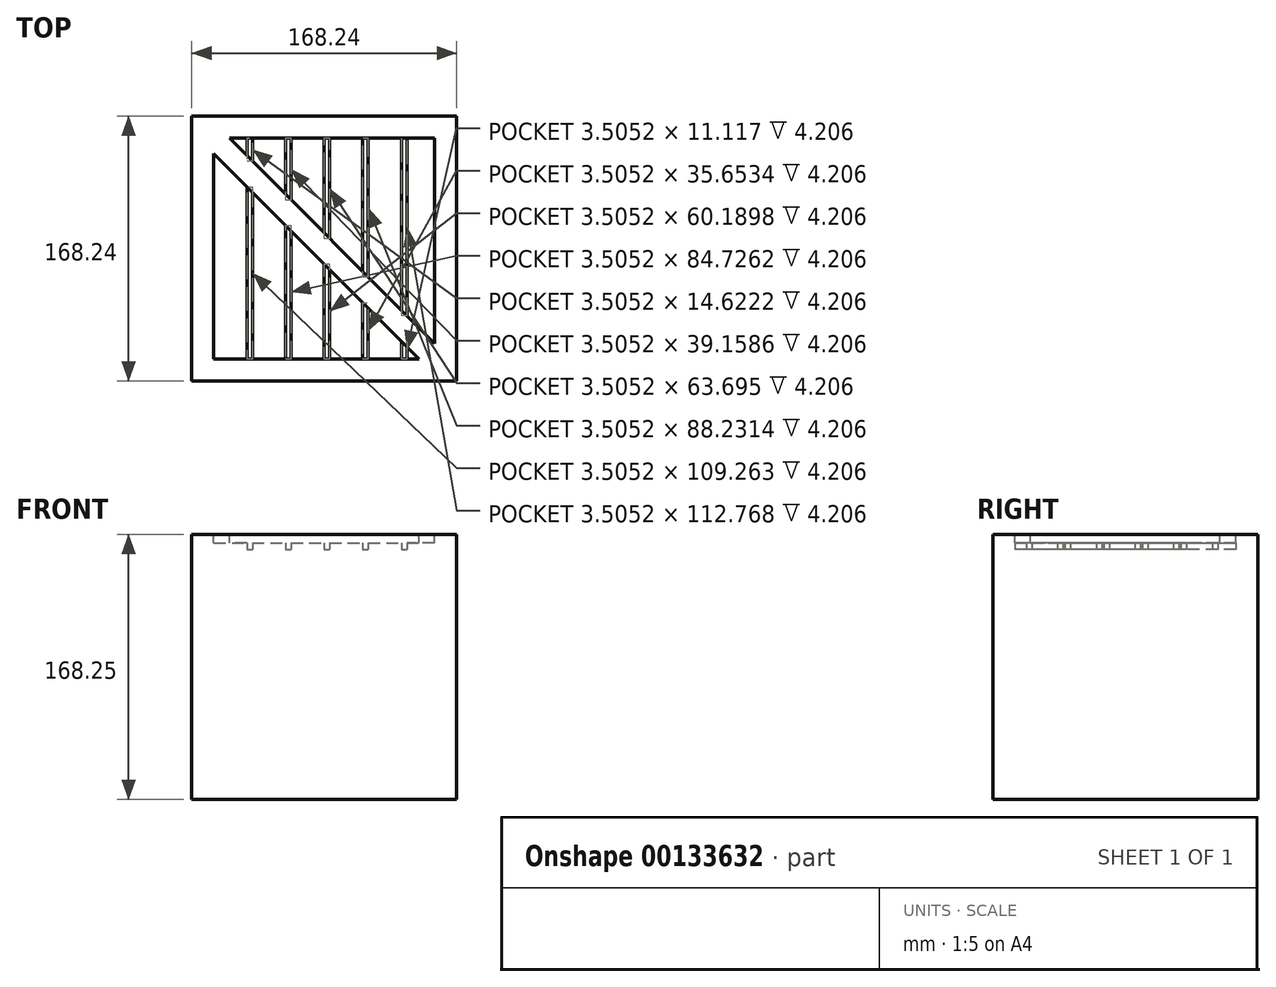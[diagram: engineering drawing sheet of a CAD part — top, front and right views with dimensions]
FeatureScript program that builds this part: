
annotation { "Feature Type Name" : "Feature", "Feature Type Description" : "" }
export const myFeature = defineFeature(function(context is Context, id is Id, definition is map)
    precondition{}
    {
        {
            var Q0;
            Q0=qCreatedBy(makeId("Top.planeOp"),FACE);
            var sketch = newSketch(context, id + "F0", { "sketchPlane" : qUnion([Q0])});
            skLineSegment(sketch, "E0.bottom", {"start": v(609.6, 609.6) * mm, "end": v(-609.6, 609.6) * mm});
            skLineSegment(sketch, "E0.top", {"start": v(609.6, -609.6) * mm, "end": v(-609.6, -609.6) * mm});
            skLineSegment(sketch, "E0.left", {"start": v(609.6, 609.6) * mm, "end": v(609.6, -609.6) * mm});
            skLineSegment(sketch, "E0.right", {"start": v(-609.6, 609.6) * mm, "end": v(-609.6, -609.6) * mm});
            skPoint(sketch, "E0.middle", {"position": v(0, 0) * mm});
            skSolve(sketch);
        }
        {
            var Q0;
            Q0=qSketchRegion(id+"F0",true);
            extrude(context, id + "F1", {"entities" : qUnion([Q0]), "depth" : 1219.2 * mm});
        }
        {
            var Q0;
            Q0=makeQuery(id+"F1.opExtrude","CAP_FACE",FACE,{"disambiguationData":[OSD([sQuery(id+"F0.wireOp",EDGE,"E0.bottom"),sQuery(id+"F0.wireOp",EDGE,"E0.top"),sQuery(id+"F0.wireOp",EDGE,"E0.left"),sQuery(id+"F0.wireOp",EDGE,"E0.right")])],"isStart":false});
            var sketch = newSketch(context, id + "F2", { "sketchPlane" : qUnion([Q0])});
            skLineSegment(sketch, "E1.0", {"start": v(508, -508) * mm, "end": v(508, 508) * mm});
            skLineSegment(sketch, "E1.1", {"start": v(-508, -508) * mm, "end": v(508, -508) * mm});
            skLineSegment(sketch, "E1.2", {"start": v(-508, 508) * mm, "end": v(-508, -508) * mm});
            skLineSegment(sketch, "E1.3", {"start": v(508, 508) * mm, "end": v(-508, 508) * mm});
            skSolve(sketch);
        }
        {
            var Q0;
            Q0=qSketchRegion(id+"F2",true);
            extrude(context, id + "F3", {"entities" : qUnion([Q0]), "operationType" : NewBodyOperationType.REMOVE, "oppositeDirection" : true, "depth" : 69.85 * mm});
        }
        {
            var Q0;
            Q0=makeQuery(id+"F1.opExtrude","CAP_FACE",FACE,{"disambiguationData":[OSD([sQuery(id+"F0.wireOp",EDGE,"E0.bottom"),sQuery(id+"F0.wireOp",EDGE,"E0.top"),sQuery(id+"F0.wireOp",EDGE,"E0.left"),sQuery(id+"F0.wireOp",EDGE,"E0.right")])],"isStart":false});
            var sketch = newSketch(context, id + "F4", { "sketchPlane" : qUnion([Q0])});
            skLineSegment(sketch, "E2", {"start": v(-436.16, 508) * mm, "end": v(508, -436.16) * mm});
            skLineSegment(sketch, "E3", {"start": v(-508, 436.16) * mm, "end": v(436.16, -508) * mm});
            skLineSegment(sketch, "E4", {"start": v(-436.16, 508) * mm, "end": v(-508, 508) * mm});
            skLineSegment(sketch, "E5", {"start": v(-508, 508) * mm, "end": v(-508, 436.16) * mm});
            skLineSegment(sketch, "E6", {"start": v(436.16, -508) * mm, "end": v(508, -508) * mm});
            skLineSegment(sketch, "E7", {"start": v(508, -508) * mm, "end": v(508, -436.16) * mm});
            skSolve(sketch);
        }
        {
            var Q0;
            Q0=makeQuery(id+"F4.imprint","IMPRINT",FACE,{"disambiguationData":[TD([[makeQuery(id+"F4.imprint","IMPRINT",EDGE,{"derivedFrom":sQuery(id+"F4.wireOp",EDGE,"E2")}),-1.0]])]});
            extrude(context, id + "F5", {"entities" : qUnion([Q0]), "oppositeDirection" : true, "depth" : 69.85 * mm});
        }
        {
            var Q0;
            Q0=makeQuery(id+"F3.boolean.opBoolean","COPY",FACE,{"derivedFrom":makeQuery(id+"F3.opExtrude","CAP_FACE",FACE,{"disambiguationData":[OSD([sQuery(id+"F2.wireOp",EDGE,"E1.0"),sQuery(id+"F2.wireOp",EDGE,"E1.1"),sQuery(id+"F2.wireOp",EDGE,"E1.2"),sQuery(id+"F2.wireOp",EDGE,"E1.3")])],"isStart":false})});
            var sketch = newSketch(context, id + "F6", { "sketchPlane" : qUnion([Q0])});
            skLineSegment(sketch, "E8.bottom", {"start": v(-508, 508) * mm, "end": v(-355.6, 508) * mm});
            skLineSegment(sketch, "E8.top", {"start": v(-508, -508) * mm, "end": v(-355.6, -508) * mm});
            skLineSegment(sketch, "E8.left", {"start": v(-508, 508) * mm, "end": v(-508, -508) * mm});
            skLineSegment(sketch, "E8.right", {"start": v(-355.6, 508) * mm, "end": v(-355.6, -508) * mm});
            skLineSegment(sketch, "E9.1.0.0", {"start": v(-330.2, 508) * mm, "end": v(-330.2, -508) * mm});
            skLineSegment(sketch, "E9.1.0.1", {"start": v(-177.8, 508) * mm, "end": v(-177.8, -508) * mm});
            skLineSegment(sketch, "E9.2.0.0", {"start": v(-152.4, 508) * mm, "end": v(-152.4, -508) * mm});
            skLineSegment(sketch, "E9.2.0.1", {"start": v(0, 508) * mm, "end": v(0, -508) * mm});
            skLineSegment(sketch, "E9.3.0.0", {"start": v(25.4, 508) * mm, "end": v(25.4, -508) * mm});
            skLineSegment(sketch, "E9.3.0.1", {"start": v(177.8, 508) * mm, "end": v(177.8, -508) * mm});
            skLineSegment(sketch, "E9.4.0.0", {"start": v(203.2, 508) * mm, "end": v(203.2, -508) * mm});
            skLineSegment(sketch, "E9.4.0.1", {"start": v(355.6, 508) * mm, "end": v(355.6, -508) * mm});
            skLineSegment(sketch, "E9.5.0.0", {"start": v(381, 508) * mm, "end": v(381, -508) * mm});
            skLineSegment(sketch, "E9.5.0.1", {"start": v(533.4, 508) * mm, "end": v(533.4, -508) * mm});
            skLineSegment(sketch, "E9.direction1", {"start": v(-508, -508) * mm, "end": v(-330.2, -508) * mm, "construction": true});
            skSolve(sketch);
        }
        {
            var Q0;
            Q0=qSketchRegion(id+"F6",true);
            var Q1;
            {var subQ0=sQuery(id+"F6.wireOp",EDGE,"E9.1.0.0");Q1=makeQuery(id+"F6.imprint","IMPRINT",FACE,{"disambiguationData":[TD([[makeQuery(id+"F6.imprint","IMPRINT",EDGE,{"derivedFrom":subQ0}),1.0]])]});}
            var Q2;
            {var subQ0=sQuery(id+"F6.wireOp",EDGE,"E9.2.0.0");Q2=makeQuery(id+"F6.imprint","IMPRINT",FACE,{"disambiguationData":[TD([[makeQuery(id+"F6.imprint","IMPRINT",EDGE,{"derivedFrom":subQ0}),1.0]])]});}
            var Q3;
            {var subQ0=sQuery(id+"F6.wireOp",EDGE,"E9.3.0.0");Q3=makeQuery(id+"F6.imprint","IMPRINT",FACE,{"disambiguationData":[TD([[makeQuery(id+"F6.imprint","IMPRINT",EDGE,{"derivedFrom":subQ0}),1.0]])]});}
            var Q4;
            {var subQ0=sQuery(id+"F6.wireOp",EDGE,"E9.4.0.0");Q4=makeQuery(id+"F6.imprint","IMPRINT",FACE,{"disambiguationData":[TD([[makeQuery(id+"F6.imprint","IMPRINT",EDGE,{"derivedFrom":subQ0}),1.0]])]});}
            var Q5;
            {var subQ0=sQuery(id+"F6.wireOp",EDGE,"E9.5.0.0");Q5=makeQuery(id+"F6.imprint","IMPRINT",FACE,{"disambiguationData":[TD([[makeQuery(id+"F6.imprint","IMPRINT",EDGE,{"derivedFrom":subQ0}),1.0]])]});}
            extrude(context, id + "F7", {"entities" : qUnion([Q0, Q1, Q2, Q3, Q4, Q5]), "operationType" : NewBodyOperationType.ADD, "depth" : 30.48 * mm});
        }
        {
            var Q0;
            Q0=makeQuery(id+"F7.boolean.opBoolean","MERGE",FACE,{"derivedFrom":[makeQuery(id+"F1.opExtrude","CAP_FACE",FACE,{"disambiguationData":[OSD([sQuery(id+"F0.wireOp",EDGE,"E0.bottom"),sQuery(id+"F0.wireOp",EDGE,"E0.top"),sQuery(id+"F0.wireOp",EDGE,"E0.left"),sQuery(id+"F0.wireOp",EDGE,"E0.right")])],"isStart":false}),makeQuery(id+"F5.opExtrude","CAP_FACE",FACE,{"disambiguationData":[OSD([sQuery(id+"F4.wireOp",EDGE,"E2"),sQuery(id+"F4.wireOp",EDGE,"E3"),sQuery(id+"F4.wireOp",EDGE,"E4"),sQuery(id+"F4.wireOp",EDGE,"E5"),sQuery(id+"F4.wireOp",EDGE,"E6"),sQuery(id+"F4.wireOp",EDGE,"E7")])],"isStart":true})]});
            cPlane(context, id + "F8", {"entities" : qUnion([Q0]), "cplaneType" : CPlaneType.OFFSET, "offset" : 609.6 * mm, "oppositeDirection" : true, "width" : 152.4 * mm, "height" : 152.4 * mm});
        }
        {
            var Q0;
            Q0=qCreatedBy(id+"F8.planeOp",FACE);
            var sketch = newSketch(context, id + "F9", { "sketchPlane" : qUnion([Q0])});
            skLineSegment(sketch, "E10", {"start": v(0, 0) * mm, "end": v(-960.31, 0) * mm});
            skLineSegment(sketch, "E11", {"start": v(0, 0) * mm, "end": v(0, -833.57) * mm});
            skSolve(sketch);
        }
        {
            var Q0;
            Q0=makeQuery(id+"F1.opExtrude","SWEPT_BODY",BODY,{"disambiguationData":[OSD([sQuery(id+"F0.wireOp",EDGE,"E0.bottom"),sQuery(id+"F0.wireOp",EDGE,"E0.top"),sQuery(id+"F0.wireOp",EDGE,"E0.left"),sQuery(id+"F0.wireOp",EDGE,"E0.right")])]});
            var Q1;
            Q1=qCreatedBy(makeId("Origin.pointOp"),VERTEX);
            transform(context, id + "F10", {"entities" : qUnion([Q0]), "transformType" : TransformType.SCALE_UNIFORMLY, "scale" : .138, "scalePoint" : qUnion([Q1]), "makeCopy" : false});
        }
    });
